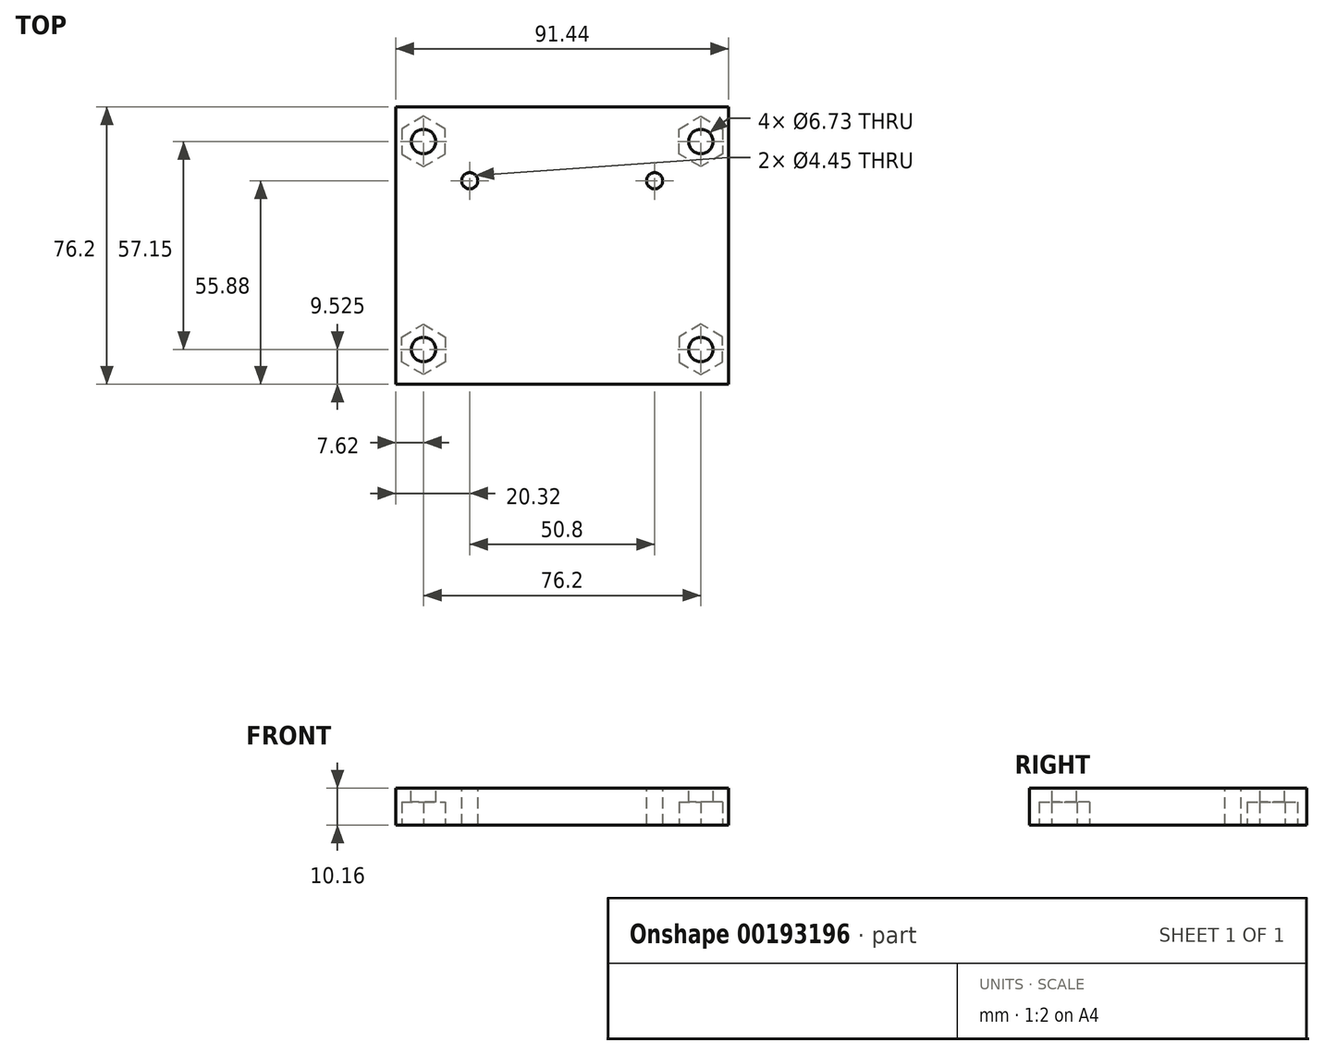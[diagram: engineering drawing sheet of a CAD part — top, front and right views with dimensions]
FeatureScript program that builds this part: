
annotation { "Feature Type Name" : "Feature", "Feature Type Description" : "" }
export const myFeature = defineFeature(function(context is Context, id is Id, definition is map)
    precondition{}
    {
        {
            var Q0;
            Q0=qCreatedBy(makeId("Top.planeOp"),FACE);
            var sketch = newSketch(context, id + "F0", { "sketchPlane" : qUnion([Q0])});
            skLineSegment(sketch, "E0.bottom", {"start": v(45.72, 38.1) * mm, "end": v(-45.72, 38.1) * mm});
            skLineSegment(sketch, "E0.top", {"start": v(45.72, -38.1) * mm, "end": v(-45.72, -38.1) * mm});
            skLineSegment(sketch, "E0.left", {"start": v(45.72, 38.1) * mm, "end": v(45.72, -38.1) * mm});
            skLineSegment(sketch, "E0.right", {"start": v(-45.72, 38.1) * mm, "end": v(-45.72, -38.1) * mm});
            skPoint(sketch, "E0.middle", {"position": v(0, 0) * mm});
            skLineSegment(sketch, "E1", {"start": v(0, -57.88) * mm, "end": v(0, -57.88) * mm});
            skPoint(sketch, "E1.endSnap0", {"position": v(0, -38.1) * mm});
            skLineSegment(sketch, "E2", {"start": v(0, 56.54) * mm, "end": v(0, -61.58) * mm, "construction": true});
            skSolve(sketch);
        }
        {
            var Q0;
            Q0=makeQuery(id+"F0.imprint","IMPRINT",FACE,{"disambiguationData":[TD([[makeQuery(id+"F0.imprint","IMPRINT",EDGE,{"derivedFrom":sQuery(id+"F0.wireOp",EDGE,"E0.bottom")}),1.0]])]});
            extrude(context, id + "F1", {"entities" : qUnion([Q0]), "depth" : 10.16 * mm});
        }
        {
            var Q0;
            Q0=makeQuery(id+"F1.opExtrude","CAP_FACE",FACE,{"disambiguationData":[OSD([sQuery(id+"F0.wireOp",EDGE,"E0.bottom"),sQuery(id+"F0.wireOp",EDGE,"E0.top"),sQuery(id+"F0.wireOp",EDGE,"E0.left"),sQuery(id+"F0.wireOp",EDGE,"E0.right")])],"isStart":false});
            var sketch = newSketch(context, id + "F2", { "sketchPlane" : qUnion([Q0])});
            skLineSegment(sketch, "E3", {"start": v(-84, 17.78) * mm, "end": v(85.16, 17.78) * mm, "construction": true});
            skLineSegment(sketch, "E4", {"start": v(0, 62.75) * mm, "end": v(0, -51.89) * mm, "construction": true});
            skCircle(sketch, "E5", {"center": v(-25.4, 17.78) * mm, "radius": 2.08 * mm});
            skCircle(sketch, "E6.MirrorC", {"center": v(25.4, 17.78) * mm, "radius": 2.08 * mm});
            skSolve(sketch);
        }
        {
            var Q0;
            Q0=sQuery(id+"F2.wireOp",VERTEX,"E5.center");
            var Q1;
            Q1=sQuery(id+"F2.wireOp",VERTEX,"E6.MirrorC.center");
            var Q2;
            Q2=makeQuery(id+"F1.opExtrude","SWEPT_BODY",BODY,{"disambiguationData":[OSD([sQuery(id+"F0.wireOp",EDGE,"E0.bottom"),sQuery(id+"F0.wireOp",EDGE,"E0.top"),sQuery(id+"F0.wireOp",EDGE,"E0.left"),sQuery(id+"F0.wireOp",EDGE,"E0.right")])]});
            hole(context, id + "F3", {"style" : HoleStyle.SIMPLE, "endStyle" : HoleEndStyle.THROUGH, "holeDiameter" : 4.44 * mm, "locations" : qUnion([Q0, Q1]), "scope" : qUnion([Q2]), "isTappedThrough" : true});
        }
        {
            var Q0;
            Q0=makeQuery(id+"F2.imprint","IMPRINT",FACE,{"disambiguationData":[TD([[makeQuery(id+"F2.imprint","IMPRINT",EDGE,{"derivedFrom":sQuery(id+"F2.wireOp",EDGE,"E5")}),-1.0]])]});
            var sketch = newSketch(context, id + "F4", { "sketchPlane" : qUnion([Q0])});
            skLineSegment(sketch, "E7", {"start": v(-53.77, 28.58) * mm, "end": v(65.38, 28.58) * mm, "construction": true});
            skCircle(sketch, "E8", {"center": v(-38.1, 28.58) * mm, "radius": 3.18 * mm});
            skCircle(sketch, "E9.MirrorC", {"center": v(38.1, 28.58) * mm, "radius": 3.18 * mm});
            skLineSegment(sketch, "E10", {"start": v(-56.57, 0) * mm, "end": v(56.57, 0) * mm, "construction": true});
            skCircle(sketch, "E11.MirrorC", {"center": v(-38.1, -28.58) * mm, "radius": 3.18 * mm});
            skCircle(sketch, "E12.MirrorC", {"center": v(38.1, -28.58) * mm, "radius": 3.18 * mm});
            skSolve(sketch);
        }
        {
            var Q0;
            Q0=sQuery(id+"F4.wireOp",VERTEX,"E8.center");
            var Q1;
            Q1=sQuery(id+"F4.wireOp",VERTEX,"E9.MirrorC.center");
            var Q2;
            Q2=sQuery(id+"F4.wireOp",VERTEX,"E11.MirrorC.center");
            var Q3;
            Q3=sQuery(id+"F4.wireOp",VERTEX,"E12.MirrorC.center");
            var Q4;
            Q4=makeQuery(id+"F1.opExtrude","SWEPT_BODY",BODY,{"disambiguationData":[OSD([sQuery(id+"F0.wireOp",EDGE,"E0.bottom"),sQuery(id+"F0.wireOp",EDGE,"E0.top"),sQuery(id+"F0.wireOp",EDGE,"E0.left"),sQuery(id+"F0.wireOp",EDGE,"E0.right")])]});
            hole(context, id + "F5", {"style" : HoleStyle.SIMPLE, "endStyle" : HoleEndStyle.THROUGH, "holeDiameter" : 6.73 * mm, "locations" : qUnion([Q0, Q1, Q2, Q3]), "scope" : qUnion([Q4]), "isTappedThrough" : true});
        }
        {
            var Q0;
            Q0=makeQuery(id+"F0.imprint","IMPRINT",FACE,{"disambiguationData":[TD([[makeQuery(id+"F0.imprint","IMPRINT",EDGE,{"derivedFrom":sQuery(id+"F0.wireOp",EDGE,"E0.bottom")}),1.0]])]});
            var sketch = newSketch(context, id + "F6", { "sketchPlane" : qUnion([Q0])});
            skCircle(sketch, "E13", {"center": v(38.1, 28.58) * mm, "radius": 6.93 * mm, "construction": true});
            skLineSegment(sketch, "E14.0", {"start": v(32.1, 32.04) * mm, "end": v(38.1, 35.5) * mm});
            skLineSegment(sketch, "E14.1", {"start": v(38.1, 35.5) * mm, "end": v(44.1, 32.04) * mm});
            skLineSegment(sketch, "E14.2", {"start": v(44.1, 32.04) * mm, "end": v(44.1, 25.11) * mm});
            skLineSegment(sketch, "E14.3", {"start": v(44.1, 25.11) * mm, "end": v(38.1, 21.65) * mm});
            skLineSegment(sketch, "E14.4", {"start": v(38.1, 21.65) * mm, "end": v(32.1, 25.11) * mm});
            skLineSegment(sketch, "E14.5", {"start": v(32.1, 25.11) * mm, "end": v(32.1, 32.04) * mm});
            skLineSegment(sketch, "E15", {"start": v(70.84, 28.58) * mm, "end": v(-61.33, 28.57) * mm, "construction": true});
            skLineSegment(sketch, "E16", {"start": v(38.1, 54.07) * mm, "end": v(38.1, -53.13) * mm, "construction": true});
            skLineSegment(sketch, "E17.MirrorCS", {"start": v(-38.1, 21.65) * mm, "end": v(-32.1, 25.11) * mm});
            skLineSegment(sketch, "E18.MirrorCS", {"start": v(-70.84, 28.57) * mm, "end": v(61.33, 28.58) * mm, "construction": true});
            skLineSegment(sketch, "E19.MirrorCS", {"start": v(-32.1, 25.11) * mm, "end": v(-32.1, 32.04) * mm});
            skLineSegment(sketch, "E20.MirrorCS", {"start": v(-32.1, 32.04) * mm, "end": v(-38.1, 35.5) * mm});
            skLineSegment(sketch, "E21.MirrorCS", {"start": v(-38.1, 35.5) * mm, "end": v(-44.1, 32.04) * mm});
            skLineSegment(sketch, "E22.MirrorCS", {"start": v(-44.1, 32.04) * mm, "end": v(-44.1, 25.11) * mm});
            skLineSegment(sketch, "E23.MirrorCS", {"start": v(-44.1, 25.11) * mm, "end": v(-38.1, 21.65) * mm});
            skLineSegment(sketch, "E24.MirrorCS", {"start": v(38.1, -21.65) * mm, "end": v(32.1, -25.11) * mm});
            skLineSegment(sketch, "E25.MirrorCS", {"start": v(44.1, -25.11) * mm, "end": v(38.1, -21.65) * mm});
            skLineSegment(sketch, "E26.MirrorCS", {"start": v(-70.84, -28.58) * mm, "end": v(61.33, -28.57) * mm, "construction": true});
            skLineSegment(sketch, "E27.MirrorCS", {"start": v(44.1, -32.04) * mm, "end": v(44.1, -25.11) * mm});
            skLineSegment(sketch, "E28.MirrorCS", {"start": v(38.1, -35.5) * mm, "end": v(44.1, -32.04) * mm});
            skLineSegment(sketch, "E29.MirrorCS", {"start": v(32.1, -32.04) * mm, "end": v(38.1, -35.5) * mm});
            skLineSegment(sketch, "E30.MirrorCS", {"start": v(32.1, -25.11) * mm, "end": v(32.1, -32.04) * mm});
            skLineSegment(sketch, "E31.MirrorCS", {"start": v(-38.1, -21.65) * mm, "end": v(-32.1, -25.11) * mm});
            skLineSegment(sketch, "E32.MirrorCS", {"start": v(-32.1, -25.11) * mm, "end": v(-32.1, -32.04) * mm});
            skLineSegment(sketch, "E33.MirrorCS", {"start": v(-44.1, -25.11) * mm, "end": v(-38.1, -21.65) * mm});
            skLineSegment(sketch, "E34.MirrorCS", {"start": v(-44.1, -32.04) * mm, "end": v(-44.1, -25.11) * mm});
            skLineSegment(sketch, "E35.MirrorCS", {"start": v(-38.1, -35.5) * mm, "end": v(-44.1, -32.04) * mm});
            skLineSegment(sketch, "E36.MirrorCS", {"start": v(-32.1, -32.04) * mm, "end": v(-38.1, -35.5) * mm});
            skSolve(sketch);
        }
        {
            var Q0;
            Q0 = qSketchRegion(id + "F6", true);
            extrude(context, id + "F7", {"entities" : qUnion([Q0]), "operationType" : NewBodyOperationType.REMOVE, "depth" : 6.35 * mm});
        }
    });
